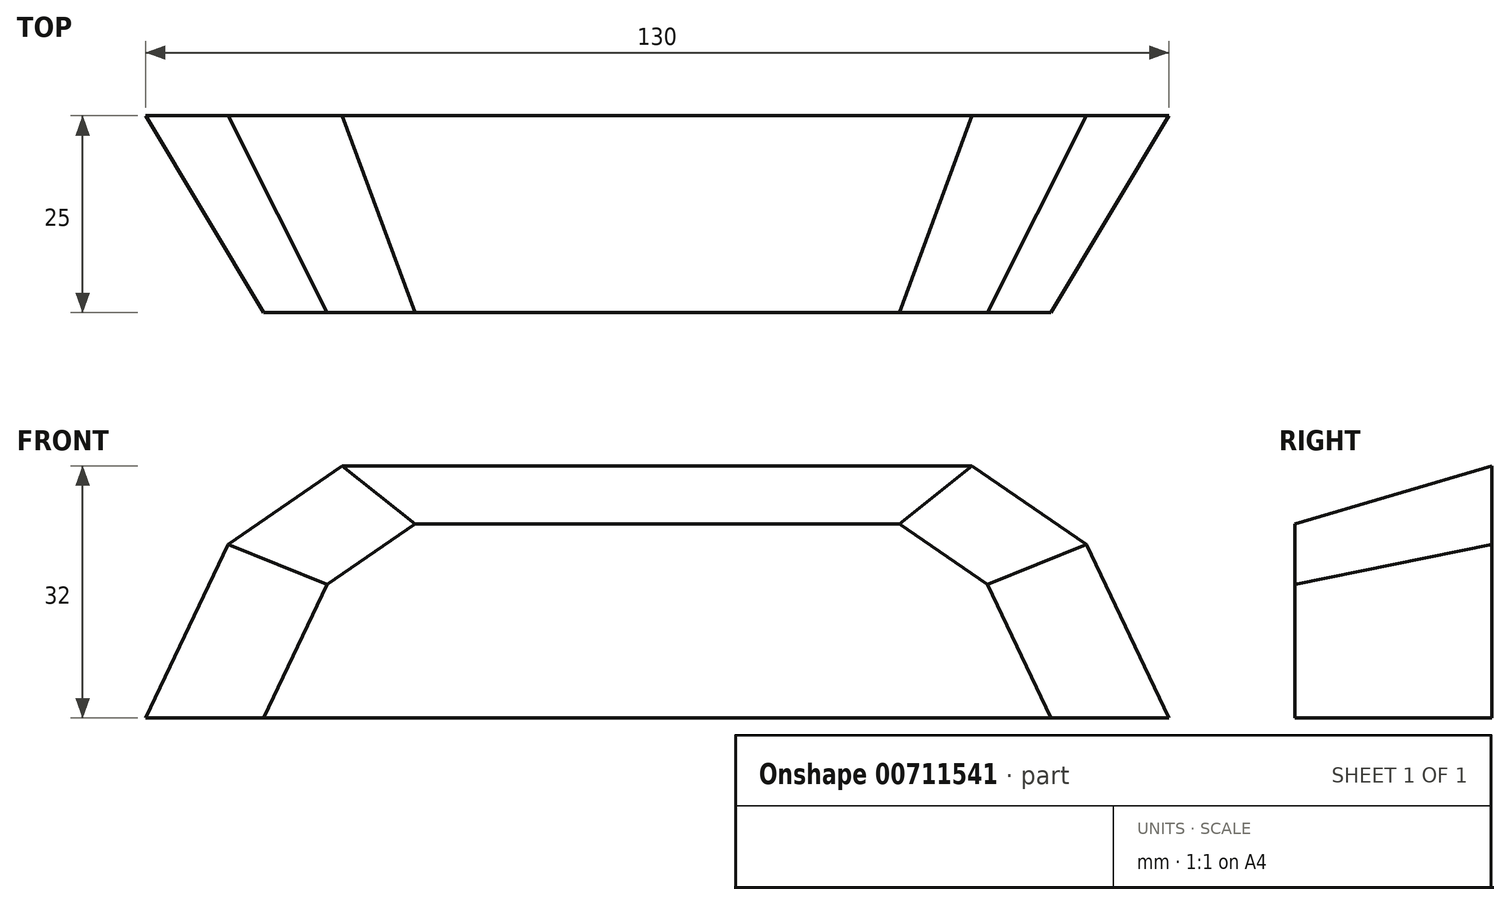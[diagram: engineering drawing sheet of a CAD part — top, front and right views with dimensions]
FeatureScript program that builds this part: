
annotation { "Feature Type Name" : "Feature", "Feature Type Description" : "" }
export const myFeature = defineFeature(function(context is Context, id is Id, definition is map)
    precondition{}
    {
        {
            var Q0;
            Q0=qCreatedBy(makeId("Front.planeOp"),FACE);
            cPlane(context, id + "F0", {"entities" : qUnion([Q0]), "cplaneType" : CPlaneType.OFFSET, "offset" : 80 * mm, "width" : 152.4 * mm, "height" : 152.4 * mm});
        }
        {
            var Q0;
            Q0=qCreatedBy(id+"F0.planeOp",FACE);
            var sketch = newSketch(context, id + "F1", { "sketchPlane" : qUnion([Q0])});
            skLineSegment(sketch, "E0", {"start": v(-65, 0) * mm, "end": v(-54.5, 22) * mm});
            skLineSegment(sketch, "E1", {"start": v(65, 0) * mm, "end": v(-65, 0) * mm});
            skLineSegment(sketch, "E2", {"start": v(-54.5, 22) * mm, "end": v(-40, 32) * mm});
            skLineSegment(sketch, "E3", {"start": v(-40, 32) * mm, "end": v(0, 32) * mm});
            skLineSegment(sketch, "E4.MirrorCS", {"start": v(40, 32) * mm, "end": v(0, 32) * mm});
            skLineSegment(sketch, "E5.MirrorCS", {"start": v(54.5, 22) * mm, "end": v(40, 32) * mm});
            skLineSegment(sketch, "E6.MirrorCS", {"start": v(65, 0) * mm, "end": v(54.5, 22) * mm});
            skSolve(sketch);
        }
        {
            var Q0;
            Q0=qCreatedBy(id+"F0.planeOp",FACE);
            cPlane(context, id + "F2", {"entities" : qUnion([Q0]), "cplaneType" : CPlaneType.OFFSET, "offset" : 25 * mm, "width" : 150 * mm, "height" : 150 * mm});
        }
        {
            var Q0;
            Q0=qCreatedBy(id+"F2.planeOp",FACE);
            var sketch = newSketch(context, id + "F3", { "sketchPlane" : qUnion([Q0])});
            skLineSegment(sketch, "E7", {"start": v(-50, 0) * mm, "end": v(-41.92, 16.92) * mm});
            skLineSegment(sketch, "E8", {"start": v(50, 0) * mm, "end": v(-50, 0) * mm});
            skLineSegment(sketch, "E9", {"start": v(-41.92, 16.92) * mm, "end": v(-30.77, 24.62) * mm});
            skLineSegment(sketch, "E10", {"start": v(-30.77, 24.62) * mm, "end": v(0, 24.62) * mm});
            skLineSegment(sketch, "E11.MirrorCS", {"start": v(30.77, 24.62) * mm, "end": v(0, 24.62) * mm});
            skLineSegment(sketch, "E12.MirrorCS", {"start": v(41.92, 16.92) * mm, "end": v(30.77, 24.62) * mm});
            skLineSegment(sketch, "E13.MirrorCS", {"start": v(50, 0) * mm, "end": v(41.92, 16.92) * mm});
            skSolve(sketch);
        }
        {
            var Q0;
            Q0=makeQuery(id+"F3.imprint","IMPRINT",FACE,{"disambiguationData":[TD([[makeQuery(id+"F3.imprint","IMPRINT",EDGE,{"derivedFrom":sQuery(id+"F3.wireOp",EDGE,"E7")}),-1.0]])]});
            var Q1;
            Q1=makeQuery(id+"F1.imprint","IMPRINT",FACE,{"disambiguationData":[TD([[makeQuery(id+"F1.imprint","IMPRINT",EDGE,{"derivedFrom":sQuery(id+"F1.wireOp",EDGE,"E0")}),-1.0]])]});
            loft(context, id + "F4", {"sheetProfilesArray" : [{ "sheetProfileEntities" : qUnion([Q0]) }, { "sheetProfileEntities" : qUnion([Q1]) }]});
        }
    });
